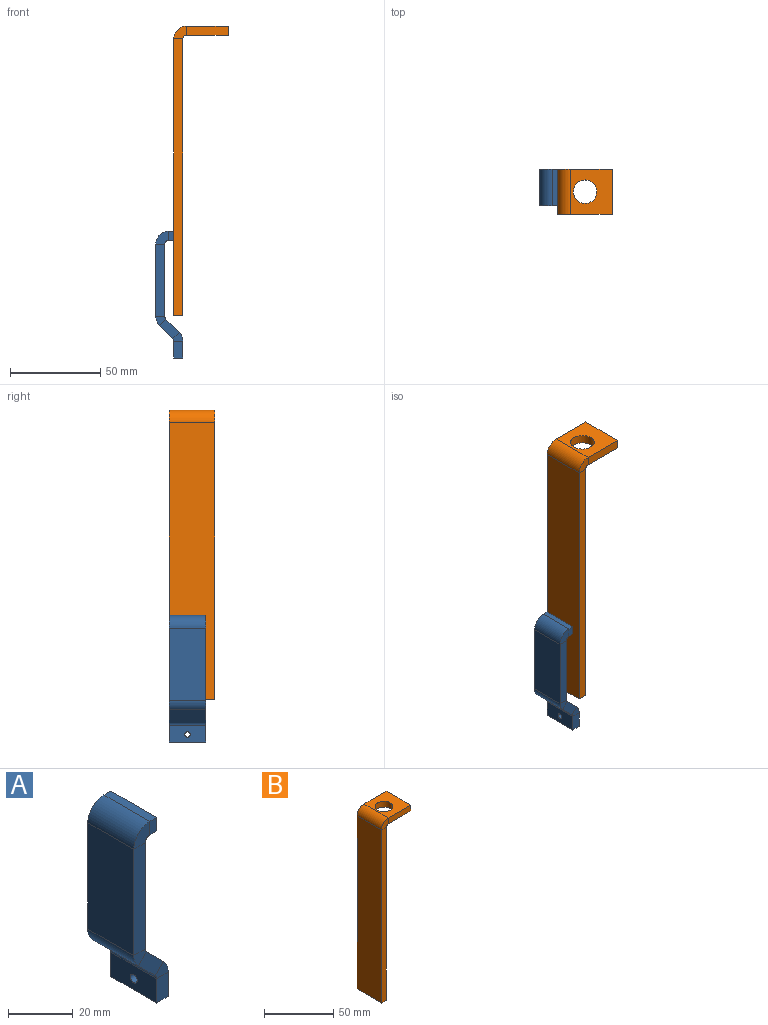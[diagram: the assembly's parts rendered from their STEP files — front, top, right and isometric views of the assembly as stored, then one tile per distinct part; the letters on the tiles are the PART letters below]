
ASSEMBLY  parts=2 mates=1
PART A: 31 faces, bbox 15x20x70 mm
  f0: plane 5x3mm, normal (0,1,0), area 15mm2, adj f2,f3,f4,f28
  f1: plane 5x3mm, normal (0,-1,0), area 15mm2, adj f2,f3,f4,f27
  f2: plane 20x5mm, normal (1,0,0), area 100mm2, adj f0,f1,f3,f4
  f3: plane 20x3mm, normal (0,0,1), area 60mm2, adj f0,f1,f2,f29
  f4: plane 20x3mm, normal (0,0,-1), area 60mm2, adj f0,f1,f2,f30
  f5: plane 40.1x5mm, normal (0,1,0), area 200.5mm2, adj f7,f8,f24,f28
  f6: plane 40.1x5mm, normal (0,-1,0), area 200.5mm2, adj f7,f8,f23,f27
  f7: plane 40.1x20mm, normal (-1,0,0), area 802mm2, adj f5,f6,f25,f29
  f8: plane 40.1x20mm, normal (1,0,0), area 802mm2, adj f5,f6,f26,f30
  f9: plane 10.9x10.9mm, normal (0,1,0), area 52.1mm2, adj f11,f12,f20,f24
  f10: plane 10.9x10.9mm, normal (0,-1,0), area 52.1mm2, adj f11,f12,f19,f23
  f11: plane 20x7.36mm, normal (-0.71,0,-0.71), area 208.3mm2, adj f9,f10,f22,f25
  f12: plane 20x7.36mm, normal (0.71,0,0.71), area 208.3mm2, adj f9,f10,f21,f26
  f13: plane 9.17x5mm, normal (0,1,0), area 45.9mm2, adj f14,f17,f18,f20
  f14: plane 20x5mm, normal (0,0,-1), area 100mm2, adj f13,f15,f17,f18
  f15: plane 9.17x5mm, normal (0,-1,0), area 45.9mm2, adj f14,f17,f18,f19
  f16: cylinder r=1.5mm len=5mm, axis (-1,0,0), area 47.1mm2, adj f17,f18
  f17: plane 20x9.17mm, normal (-1,0,0), area 176.4mm2, adj f13,f14,f15,f16,f22
  f18: plane 20x9.17mm, normal (1,0,0), area 176.4mm2, adj f13,f14,f15,f16,f21
  f19: plane 5.59x4.95mm, normal (0,-1,0), area 17.7mm2, adj f10,f15,f21,f22
  f20: plane 5.59x4.95mm, normal (0,1,0), area 17.7mm2, adj f9,f13,f21,f22
  f21: cylinder r=7mm len=20mm, axis (0,-1,0), area 110mm2, adj f12,f18,f19,f20
  f22: cylinder r=2mm len=20mm, axis (0,-1,0), area 31.4mm2, adj f11,f17,f19,f20
  f23: plane 5.59x4.95mm, normal (0,-1,0), area 17.7mm2, adj f6,f10,f25,f26
  f24: plane 5.59x4.95mm, normal (0,1,0), area 17.7mm2, adj f5,f9,f25,f26
  f25: cylinder r=7mm len=20mm, axis (0,-1,0), area 110mm2, adj f7,f11,f23,f24
  f26: cylinder r=2mm len=20mm, axis (0,-1,0), area 31.4mm2, adj f8,f12,f23,f24
  f27: plane 7x7mm, normal (0,-1,0), area 35.3mm2, adj f1,f6,f29,f30
  f28: plane 7x7mm, normal (0,1,0), area 35.3mm2, adj f0,f5,f29,f30
  f29: cylinder r=7mm len=20mm, axis (0,-1,0), area 219.9mm2, adj f3,f7,f27,f28
  f30: cylinder r=2mm len=20mm, axis (0,-1,0), area 62.8mm2, adj f4,f8,f27,f28
PART B: 15 faces, bbox 30x25x160 mm
  f0: plane 153x5mm, normal (0,1,0), area 765mm2, adj f1,f3,f4,f12
  f1: plane 25x5mm, normal (0,0,-1), area 125mm2, adj f0,f2,f3,f4
  f2: plane 153x5mm, normal (0,-1,0), area 765mm2, adj f1,f3,f4,f11
  f3: plane 153x25mm, normal (-1,0,0), area 3825mm2, adj f0,f1,f2,f13
  f4: plane 153x25mm, normal (1,0,0), area 3825mm2, adj f0,f1,f2,f14
  f5: plane 23x5mm, normal (0,1,0), area 115mm2, adj f8,f9,f10,f12
  f6: plane 23x5mm, normal (0,-1,0), area 115mm2, adj f8,f9,f10,f11
  f7: cylinder r=6.5mm len=13mm, axis (0,0,1), area 204.2mm2, adj f9,f10
  f8: plane 25x5mm, normal (1,0,0), area 125mm2, adj f5,f6,f9,f10
  f9: plane 25x23mm, normal (0,0,1), area 442.3mm2, adj f5,f6,f7,f8,f13
  f10: plane 25x23mm, normal (0,0,-1), area 442.3mm2, adj f5,f6,f7,f8,f14
  f11: plane 7x7mm, normal (0,-1,0), area 35.3mm2, adj f2,f6,f13,f14
  f12: plane 7x7mm, normal (0,1,0), area 35.3mm2, adj f0,f5,f13,f14
  f13: cylinder r=7mm len=25mm, axis (0,-1,0), area 274.9mm2, adj f3,f9,f11,f12
  f14: cylinder r=2mm len=25mm, axis (0,-1,0), area 78.5mm2, adj f4,f10,f11,f12
PLACE A t=(-9.03,-5.12,-82.41)mm
PLACE B t=(0.97,-5.12,31.09)mm
MATE fastened B.f3 <-> A.f2  axis (-1,0,0) through (0.97,-5.12,-52.41)mm
